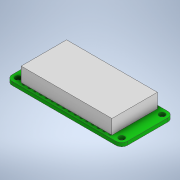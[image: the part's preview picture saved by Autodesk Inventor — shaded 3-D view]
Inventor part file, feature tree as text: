
AUTODESK INVENTOR PART (.ipt)
format: ipt  version: 2021 (Build 250183000, 183)  size: 225,280 bytes
history: native  units: in
note: dims shown in document units (in); Inventor stores cm internally (conversion verified against a paired STEP export)
features: extrude x4, sketch x4, pattern_linear x2
ambient origin geometry x8: Origin, YZ Plane, XZ Plane, XY Plane, X Axis, Y Axis, Z Axis, Center Point
bodies: Solid1 (feature_tree)
feature tree (10):
  extrude  "Extrusion1"  Depth=0.9in
  extrude  "Extrusion6"  Depth=0.1in
  pattern_linear  "Rectangular Pattern1"  Spacing1=0.1in  [1 undecoded]
  extrude  "Extrusion7"  Depth=0.1in
  pattern_linear  "Rectangular Pattern2"  Spacing1=0.1in  [1 undecoded]
  extrude  "Extrusion11"  Depth=0.1in
  sketch  "Sketch1"  dims[d0=2.0in d1=0.9in]
  sketch  "Sketch6"  dims[d2=0.1in d6=0.7in]
  sketch  "Sketch7"  dims[d9=0.35in]
  sketch  "Sketch11"  dims[d10=0.1in d11=0.1in d13=0.1in d14=0.1in d15=0.1in d16=0.063in d17=0.0in d46=0.0394in d47=0.05in d48=0.05in d49=0.0in d50=0.0in d51=6.2992in d53=0.1in d54=1.15in d55=0.05in d56=0.0394in d57=0.0in d58=0.0in d59=4.7244in d61=0.1in d77=1.5748in d78=0.7874in d79=0.25in d80=0.0in d81=0.2in]
note: 2 required parameter values undecoded (feature->parameter linkage not recoverable at this tier; creation-order binding heuristic only, values carry confidence <= 0.55)
